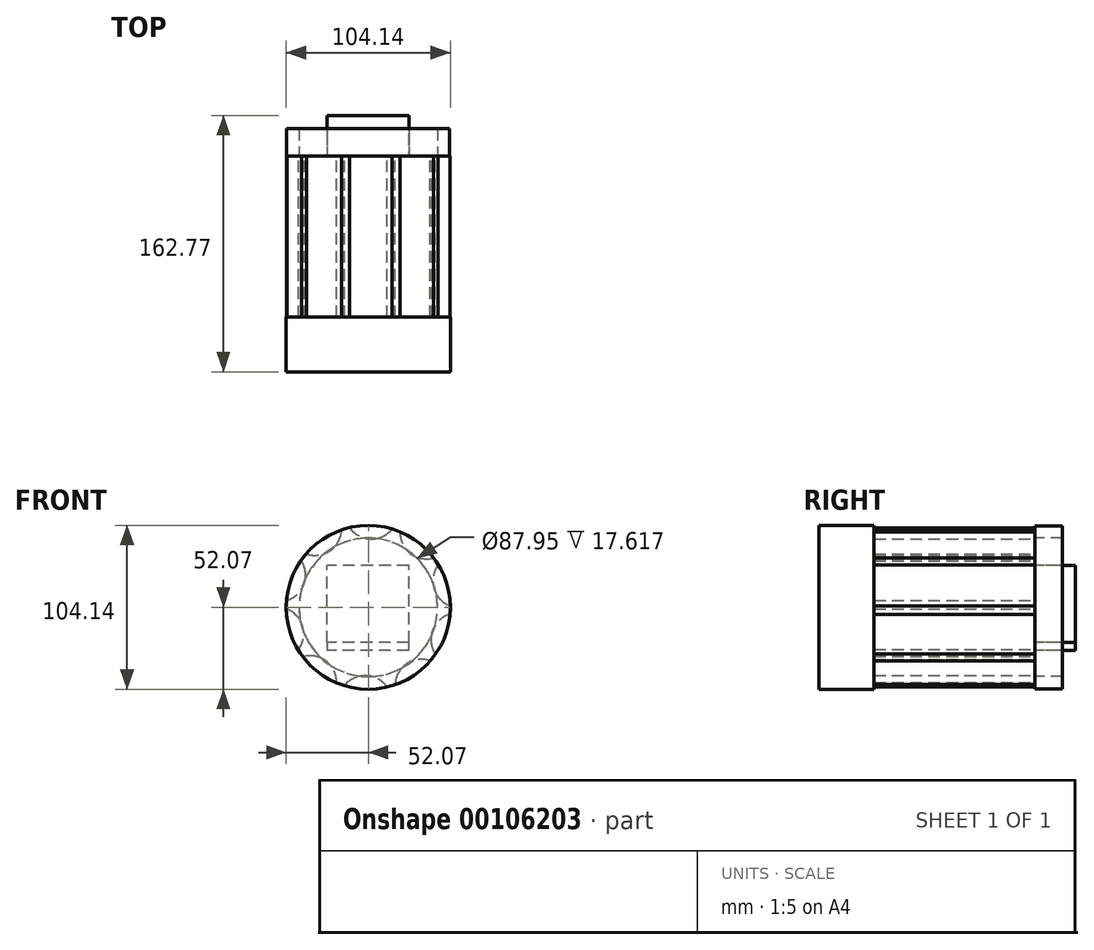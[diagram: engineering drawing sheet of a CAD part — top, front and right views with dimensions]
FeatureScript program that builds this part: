
annotation { "Feature Type Name" : "Feature", "Feature Type Description" : "" }
export const myFeature = defineFeature(function(context is Context, id is Id, definition is map)
    precondition{}
    {
        {
            var Q0;
            Q0=qCreatedBy(makeId("Front.planeOp"),FACE);
            var sketch = newSketch(context, id + "F0", { "sketchPlane" : qUnion([Q0])});
            skArc(sketch, "E0", {"start": v(-11.8, 50.47) * mm, "mid": v(-14.42, 49.79) * mm, "end": v(-17, 48.97) * mm});
            skArc(sketch, "E1", {"start": v(-11.8, 50.47) * mm, "mid": v(1.4, 43.41) * mm, "end": v(15.03, 49.61) * mm});
            skArc(sketch, "E2.1.0", {"start": v(-39.22, 33.9) * mm, "mid": v(-24.39, 35.94) * mm, "end": v(-17, 48.97) * mm});
            skArc(sketch, "E2.2.0", {"start": v(-51.65, 4.37) * mm, "mid": v(-40.86, 14.74) * mm, "end": v(-42.54, 29.62) * mm});
            skArc(sketch, "E2.3.0", {"start": v(-44.35, -26.83) * mm, "mid": v(-41.72, -12.09) * mm, "end": v(-51.83, -1.04) * mm});
            skArc(sketch, "E2.4.0", {"start": v(-20.12, -47.77) * mm, "mid": v(-26.65, -34.3) * mm, "end": v(-41.32, -31.3) * mm});
            skArc(sketch, "E2.5.0", {"start": v(11.8, -50.47) * mm, "mid": v(-1.4, -43.41) * mm, "end": v(-15.03, -49.61) * mm});
            skArc(sketch, "E2.6.0", {"start": v(39.22, -33.9) * mm, "mid": v(24.39, -35.94) * mm, "end": v(17, -48.97) * mm});
            skArc(sketch, "E2.7.0", {"start": v(51.65, -4.37) * mm, "mid": v(40.86, -14.74) * mm, "end": v(42.54, -29.62) * mm});
            skArc(sketch, "E2.8.0", {"start": v(44.35, 26.83) * mm, "mid": v(41.72, 12.09) * mm, "end": v(51.83, 1.04) * mm});
            skArc(sketch, "E2.9.0", {"start": v(20.12, 47.77) * mm, "mid": v(26.65, 34.3) * mm, "end": v(41.32, 31.3) * mm});
            skArc(sketch, "E3.trimOffspring", {"start": v(-39.22, 33.9) * mm, "mid": v(-40.93, 31.8) * mm, "end": v(-42.54, 29.62) * mm});
            skArc(sketch, "E4.trimOffspring", {"start": v(-51.65, 4.37) * mm, "mid": v(-51.8, 1.67) * mm, "end": v(-51.83, -1.04) * mm});
            skArc(sketch, "E5.trimOffspring", {"start": v(-44.35, -26.83) * mm, "mid": v(-42.9, -29.1) * mm, "end": v(-41.32, -31.3) * mm});
            skArc(sketch, "E6.trimOffspring", {"start": v(-20.12, -47.77) * mm, "mid": v(-17.6, -48.76) * mm, "end": v(-15.03, -49.61) * mm});
            skArc(sketch, "E7.trimOffspring", {"start": v(11.8, -50.47) * mm, "mid": v(14.42, -49.79) * mm, "end": v(17, -48.97) * mm});
            skArc(sketch, "E8.trimOffspring", {"start": v(39.22, -33.9) * mm, "mid": v(40.93, -31.8) * mm, "end": v(42.54, -29.62) * mm});
            skArc(sketch, "E9.trimOffspring", {"start": v(51.65, -4.37) * mm, "mid": v(51.8, -1.67) * mm, "end": v(51.83, 1.04) * mm});
            skArc(sketch, "E10.trimOffspring", {"start": v(44.35, 26.83) * mm, "mid": v(42.9, 29.1) * mm, "end": v(41.32, 31.3) * mm});
            skArc(sketch, "E11.trimOffspring", {"start": v(20.12, 47.77) * mm, "mid": v(17.6, 48.76) * mm, "end": v(15.03, 49.61) * mm});
            skSolve(sketch);
        }
        {
            var Q0;
            Q0 = qSketchRegion(id + "F0", true);
            extrude(context, id + "F1", {"entities" : qUnion([Q0]), "depth" : 67.15 * mm});
        }
        {
            var Q0;
            Q0=makeQuery(id+"F1.opExtrude","CAP_FACE",FACE,{"disambiguationData":[OSD([sQuery(id+"F0.wireOp",EDGE,"E0"),sQuery(id+"F0.wireOp",EDGE,"E1"),sQuery(id+"F0.wireOp",EDGE,"E2.1.0"),sQuery(id+"F0.wireOp",EDGE,"E2.2.0"),sQuery(id+"F0.wireOp",EDGE,"E2.3.0"),sQuery(id+"F0.wireOp",EDGE,"E2.4.0"),sQuery(id+"F0.wireOp",EDGE,"E2.5.0"),sQuery(id+"F0.wireOp",EDGE,"E2.6.0"),sQuery(id+"F0.wireOp",EDGE,"E2.7.0"),sQuery(id+"F0.wireOp",EDGE,"E2.8.0"),sQuery(id+"F0.wireOp",EDGE,"E2.9.0"),sQuery(id+"F0.wireOp",EDGE,"E3.trimOffspring"),sQuery(id+"F0.wireOp",EDGE,"E4.trimOffspring"),sQuery(id+"F0.wireOp",EDGE,"E5.trimOffspring"),sQuery(id+"F0.wireOp",EDGE,"E6.trimOffspring"),sQuery(id+"F0.wireOp",EDGE,"E7.trimOffspring"),sQuery(id+"F0.wireOp",EDGE,"E8.trimOffspring"),sQuery(id+"F0.wireOp",EDGE,"E9.trimOffspring"),sQuery(id+"F0.wireOp",EDGE,"E10.trimOffspring"),sQuery(id+"F0.wireOp",EDGE,"E11.trimOffspring")])],"isStart":false});
            var Q1;
            Q1=makeQuery(id+"F1.opExtrude","CAP_FACE",FACE,{"disambiguationData":[OSD([sQuery(id+"F0.wireOp",EDGE,"E0"),sQuery(id+"F0.wireOp",EDGE,"E1"),sQuery(id+"F0.wireOp",EDGE,"E2.1.0"),sQuery(id+"F0.wireOp",EDGE,"E2.2.0"),sQuery(id+"F0.wireOp",EDGE,"E2.3.0"),sQuery(id+"F0.wireOp",EDGE,"E2.4.0"),sQuery(id+"F0.wireOp",EDGE,"E2.5.0"),sQuery(id+"F0.wireOp",EDGE,"E2.6.0"),sQuery(id+"F0.wireOp",EDGE,"E2.7.0"),sQuery(id+"F0.wireOp",EDGE,"E2.8.0"),sQuery(id+"F0.wireOp",EDGE,"E2.9.0"),sQuery(id+"F0.wireOp",EDGE,"E3.trimOffspring"),sQuery(id+"F0.wireOp",EDGE,"E4.trimOffspring"),sQuery(id+"F0.wireOp",EDGE,"E5.trimOffspring"),sQuery(id+"F0.wireOp",EDGE,"E6.trimOffspring"),sQuery(id+"F0.wireOp",EDGE,"E7.trimOffspring"),sQuery(id+"F0.wireOp",EDGE,"E8.trimOffspring"),sQuery(id+"F0.wireOp",EDGE,"E9.trimOffspring"),sQuery(id+"F0.wireOp",EDGE,"E10.trimOffspring"),sQuery(id+"F0.wireOp",EDGE,"E11.trimOffspring")])],"isStart":true});
            extrude(context, id + "F2", {"entities" : qUnion([Q0, Q1]), "operationType" : NewBodyOperationType.ADD, "depth" : 69.8 * mm});
        }
        {
            var Q0;
            Q0=qCreatedBy(makeId("Front.planeOp"),FACE);
            var sketch = newSketch(context, id + "F3", { "sketchPlane" : qUnion([Q0])});
            skCircle(sketch, "E12", {"center": v(0, 0) * mm, "radius": 51.75 * mm});
            skCircle(sketch, "E13", {"center": v(0, 0) * mm, "radius": 43.98 * mm});
            skSolve(sketch);
        }
        {
            var Q0;
            Q0 = qSketchRegion(id + "F3", true);
            extrude(context, id + "F4", {"entities" : qUnion([Q0]), "operationType" : NewBodyOperationType.ADD, "oppositeDirection" : true, "depth" : 17.62 * mm});
        }
        {
            var Q0;
            Q0=qCreatedBy(makeId("Front.planeOp"),FACE);
            var sketch = newSketch(context, id + "F5", { "sketchPlane" : qUnion([Q0])});
            skLineSegment(sketch, "E14.bottom", {"start": v(25.9, 0) * mm, "end": v(-26.12, 0) * mm});
            skLineSegment(sketch, "E14.top", {"start": v(25.9, 26.53) * mm, "end": v(-26.12, 26.53) * mm});
            skLineSegment(sketch, "E14.left", {"start": v(25.9, 0) * mm, "end": v(25.9, 26.53) * mm});
            skLineSegment(sketch, "E14.right", {"start": v(-26.12, 0) * mm, "end": v(-26.12, 26.53) * mm});
            skLineSegment(sketch, "E15.bottom", {"start": v(25.9, -22.37) * mm, "end": v(-26.12, -22.37) * mm});
            skLineSegment(sketch, "E15.top", {"start": v(25.9, 19.66) * mm, "end": v(-26.12, 19.66) * mm});
            skLineSegment(sketch, "E15.left", {"start": v(25.9, -22.37) * mm, "end": v(25.9, 19.66) * mm});
            skLineSegment(sketch, "E15.right", {"start": v(-26.12, -22.37) * mm, "end": v(-26.12, 19.66) * mm});
            skSolve(sketch);
        }
        {
            var Q0;
            Q0 = qSketchRegion(id + "F5", true);
            extrude(context, id + "F6", {"entities" : qUnion([Q0]), "operationType" : NewBodyOperationType.ADD, "oppositeDirection" : true, "depth" : 25.73 * mm});
        }
        {
            var Q0;
            Q0=qCreatedBy(makeId("Front.planeOp"),FACE);
            var sketch = newSketch(context, id + "F7", { "sketchPlane" : qUnion([Q0])});
            skLineSegment(sketch, "E16.bottom", {"start": v(25.7, -22.37) * mm, "end": v(-26.32, -22.37) * mm});
            skLineSegment(sketch, "E16.top", {"start": v(25.7, -27.36) * mm, "end": v(-26.32, -27.36) * mm});
            skLineSegment(sketch, "E16.left", {"start": v(25.7, -22.37) * mm, "end": v(25.7, -27.36) * mm});
            skLineSegment(sketch, "E16.right", {"start": v(-26.32, -22.37) * mm, "end": v(-26.32, -27.36) * mm});
            skSolve(sketch);
        }
        {
            var Q0;
            Q0 = qSketchRegion(id + "F7", true);
            extrude(context, id + "F8", {"entities" : qUnion([Q0]), "operationType" : NewBodyOperationType.ADD, "oppositeDirection" : true, "depth" : 25.83 * mm});
        }
        {
            var Q0;
            {var subQ0=sQuery(id+"F0.wireOp",EDGE,"E11.trimOffspring");var subQ1=sQuery(id+"F0.wireOp",EDGE,"E10.trimOffspring");var subQ2=sQuery(id+"F0.wireOp",EDGE,"E9.trimOffspring");var subQ3=sQuery(id+"F0.wireOp",EDGE,"E8.trimOffspring");var subQ4=sQuery(id+"F0.wireOp",EDGE,"E7.trimOffspring");var subQ5=sQuery(id+"F0.wireOp",EDGE,"E6.trimOffspring");var subQ6=sQuery(id+"F0.wireOp",EDGE,"E5.trimOffspring");var subQ7=sQuery(id+"F0.wireOp",EDGE,"E4.trimOffspring");var subQ8=sQuery(id+"F0.wireOp",EDGE,"E3.trimOffspring");var subQ9=sQuery(id+"F0.wireOp",EDGE,"E2.9.0");var subQ10=sQuery(id+"F0.wireOp",EDGE,"E2.8.0");var subQ11=sQuery(id+"F0.wireOp",EDGE,"E2.7.0");var subQ12=sQuery(id+"F0.wireOp",EDGE,"E2.6.0");var subQ13=sQuery(id+"F0.wireOp",EDGE,"E2.5.0");var subQ14=sQuery(id+"F0.wireOp",EDGE,"E2.4.0");var subQ15=sQuery(id+"F0.wireOp",EDGE,"E2.3.0");var subQ16=sQuery(id+"F0.wireOp",EDGE,"E2.2.0");var subQ17=sQuery(id+"F0.wireOp",EDGE,"E2.1.0");var subQ18=sQuery(id+"F0.wireOp",EDGE,"E1");var subQ19=sQuery(id+"F0.wireOp",EDGE,"E0");Q0=makeQuery(id+"F2.opExtrude","CAP_FACE",FACE,{"disambiguationData":[OSD([subQ19,subQ18,subQ17,subQ16,subQ15,subQ14,subQ13,subQ12,subQ11,subQ10,subQ9,subQ8,subQ7,subQ6,subQ5,subQ4,subQ3,subQ2,subQ1,subQ0]),TDD([makeQuery(id+"F1.opExtrude","CAP_FACE",FACE,{"disambiguationData":[OSD([subQ19,subQ18,subQ17,subQ16,subQ15,subQ14,subQ13,subQ12,subQ11,subQ10,subQ9,subQ8,subQ7,subQ6,subQ5,subQ4,subQ3,subQ2,subQ1,subQ0])],"isStart":false})])],"isStart":false});}
            var sketch = newSketch(context, id + "F9", { "sketchPlane" : qUnion([Q0])});
            skCircle(sketch, "E17", {"center": v(0, 0) * mm, "radius": 52.07 * mm});
            skSolve(sketch);
        }
        {
            var Q0;
            Q0 = qSketchRegion(id + "F9", true);
            extrude(context, id + "F10", {"entities" : qUnion([Q0]), "operationType" : NewBodyOperationType.ADD, "oppositeDirection" : true, "depth" : 34.8 * mm});
        }
    });
